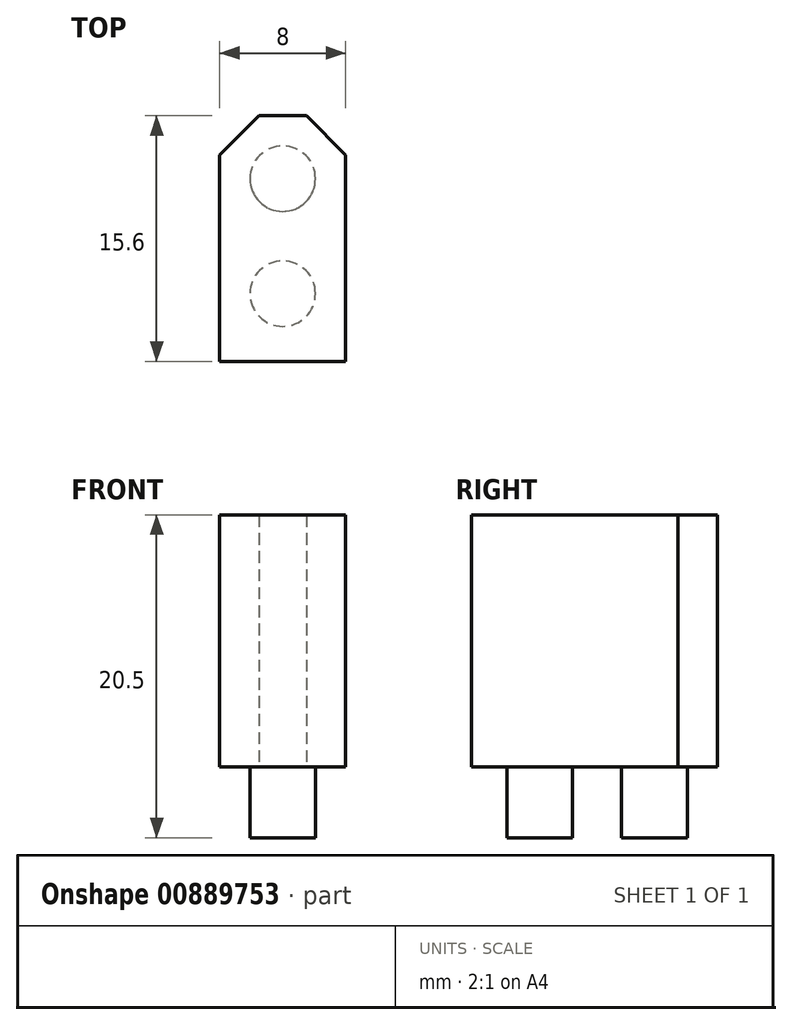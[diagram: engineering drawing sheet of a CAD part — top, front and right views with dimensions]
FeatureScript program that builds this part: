
annotation { "Feature Type Name" : "Feature", "Feature Type Description" : "" }
export const myFeature = defineFeature(function(context is Context, id is Id, definition is map)
    precondition{}
    {
        {
            var Q0;
            Q0=qCreatedBy(makeId("Top.planeOp"),FACE);
            var sketch = newSketch(context, id + "F0", { "sketchPlane" : qUnion([Q0])});
            skLineSegment(sketch, "E0.top", {"start": v(-4, 0) * mm, "end": v(4, 0) * mm});
            skLineSegment(sketch, "E0.left", {"start": v(-4, 13.1) * mm, "end": v(-4, 0) * mm});
            skLineSegment(sketch, "E0.right", {"start": v(4, 13.1) * mm, "end": v(4, 0) * mm});
            skLineSegment(sketch, "E1", {"start": v(-4, 13.1) * mm, "end": v(-1.5, 15.6) * mm});
            skLineSegment(sketch, "E2", {"start": v(-1.5, 15.6) * mm, "end": v(1.5, 15.6) * mm});
            skLineSegment(sketch, "E3", {"start": v(1.5, 15.6) * mm, "end": v(4, 13.1) * mm});
            skSolve(sketch);
        }
        {
            var Q0;
            Q0=qSketchRegion(id+"F0",true);
            extrude(context, id + "F1", {"entities" : qUnion([Q0]), "depth" : 16 * mm});
        }
        {
            var Q0;
            Q0=makeQuery(id+"F1.opExtrude","CAP_FACE",FACE,{"disambiguationData":[OSD([sQuery(id+"F0.wireOp",EDGE,"E0.top"),sQuery(id+"F0.wireOp",EDGE,"E0.left"),sQuery(id+"F0.wireOp",EDGE,"E0.right"),sQuery(id+"F0.wireOp",EDGE,"E1"),sQuery(id+"F0.wireOp",EDGE,"E2"),sQuery(id+"F0.wireOp",EDGE,"E3")])],"isStart":true});
            var sketch = newSketch(context, id + "F2", { "sketchPlane" : qUnion([Q0])});
            skCircle(sketch, "E4", {"center": v(0, -4.31) * mm, "radius": 2.08 * mm});
            skCircle(sketch, "E5", {"center": v(0, -11.61) * mm, "radius": 2.08 * mm});
            skSolve(sketch);
        }
        {
            var Q0;
            Q0=qSketchRegion(id+"F2",true);
            extrude(context, id + "F3", {"entities" : qUnion([Q0]), "operationType" : NewBodyOperationType.ADD, "depth" : 4.5 * mm});
        }
    });
